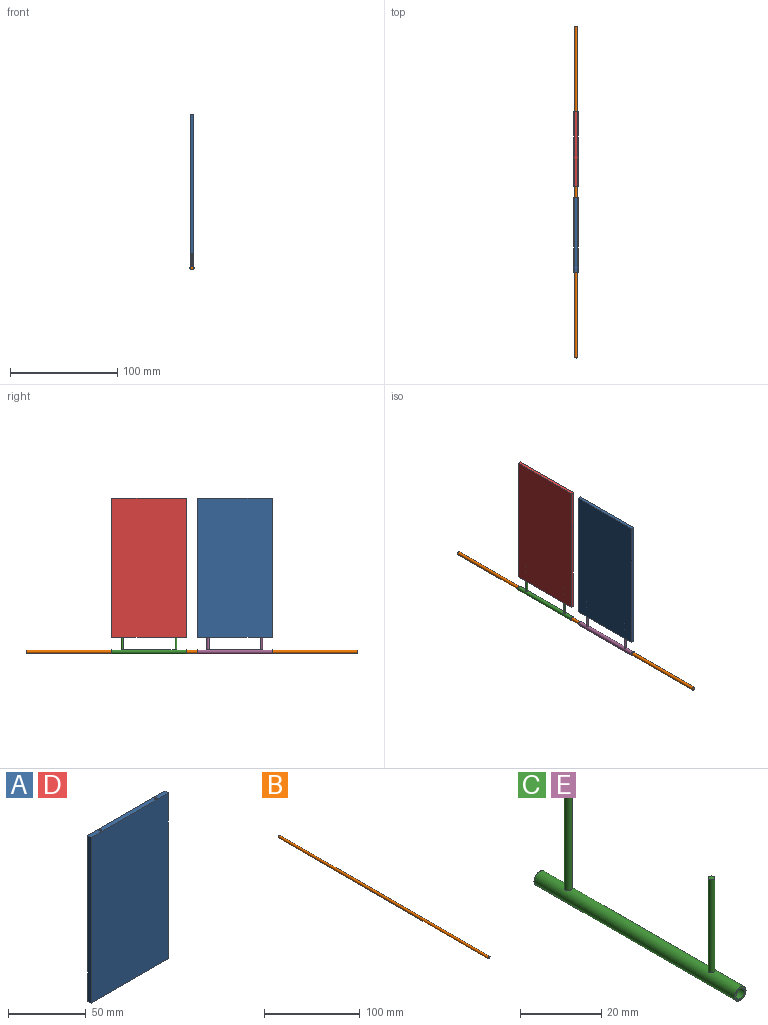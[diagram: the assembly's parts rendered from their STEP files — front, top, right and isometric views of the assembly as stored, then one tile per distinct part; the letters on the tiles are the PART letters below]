
ASSEMBLY  parts=5 mates=4
PART A: 10 faces, bbox 70x3x130 mm
  f0: plane 130x3mm, normal (1,0,0), area 390mm2, adj f1,f3,f4,f5
  f1: plane 70x3mm, normal (0,0,1), area 203.7mm2, adj f0,f2,f4,f5,f6,f8
  f2: plane 130x3mm, normal (-1,0,0), area 390mm2, adj f1,f3,f4,f5
  f3: plane 70x3mm, normal (0,0,-1), area 210mm2, adj f0,f2,f4,f5
  f4: plane 130x70mm, normal (0,-1,0), area 9100mm2, adj f0,f1,f2,f3
  f5: plane 130x70mm, normal (0,1,0), area 9100mm2, adj f0,f1,f2,f3
  f6: cylinder r=1mm len=10mm, axis (0,0,1), area 62.8mm2, adj f1,f7
  f7: plane 2x2mm, normal (0,0,1), area 3.1mm2, adj f6
  f8: cylinder r=1mm len=10mm, axis (0,0,1), area 62.8mm2, adj f1,f9
  f9: plane 2x2mm, normal (0,0,1), area 3.1mm2, adj f8
PART B: 3 faces, bbox 3x310x3 mm
  f0: cylinder r=1.5mm len=310mm, axis (0,1,0), area 2921.7mm2, adj f1,f2
  f1: plane 3x3mm, normal (0,-1,0), area 7.1mm2, adj f0
  f2: plane 3x3mm, normal (0,1,0), area 7.1mm2, adj f0
PART C: 12 faces, bbox 4x70x32 mm
  f0: cylinder r=1.5mm len=70mm, axis (0,1,0), area 654.1mm2, adj f2,f3,f6,f10
  f1: cylinder r=2mm len=70mm, axis (0,1,0), area 874.2mm2, adj f2,f3,f5,f9
  f2: plane 4x4mm, normal (0,-1,0), area 5.5mm2, adj f0,f1
  f3: plane 4x4mm, normal (0,1,0), area 5.5mm2, adj f0,f1
  f4: plane 2x2mm, normal (0,0,1), area 3.1mm2, adj f5
  f5: cylinder r=1mm len=28.27mm, axis (0,0,-1), area 176.8mm2, adj f1,f4
  f6: cylinder r=1mm len=2mm, axis (0,0,-1), area 8.3mm2, adj f0,f7
  f7: plane 2x2mm, normal (0,0,-1), area 3.1mm2, adj f6
  f8: plane 1.67x1.67mm, normal (0,0,1), area 2.2mm2, adj f9
  f9: cylinder r=0.83mm len=28.18mm, axis (0,0,-1), area 147.2mm2, adj f1,f8
  f10: cylinder r=0.83mm len=1.67mm, axis (0,0,-1), area 7.2mm2, adj f0,f11
  f11: plane 1.67x1.67mm, normal (0,0,-1), area 2.2mm2, adj f10
PART D: same geometry as A
PART E: same geometry as C
PLACE A rot(axis=(0.71,0.71,0),180deg) t=(14.85,-200.42,30.48)mm
PLACE B t=(13.35,-5.42,-48.02)mm
PLACE C t=(13.35,-85.42,-48.02)mm
PLACE D rot(axis=(0.71,0.71,0),180deg) t=(14.85,-120.42,30.48)mm
PLACE E t=(13.35,-165.42,-48.02)mm
MATE fastened E.f0 <-> B.f0  axis (0,1,0) through (13.35,-165.42,-48.02)mm
MATE fastened A.f8 <-> E.f5  axis (0,0,-1) through (13.35,-175.42,-34.52)mm
MATE fastened D.f8 <-> C.f5  axis (0,0,-1) through (13.35,-95.42,-34.52)mm
MATE fastened C.f0 <-> B.f0  axis (0,1,0) through (13.35,-155.42,-48.02)mm
